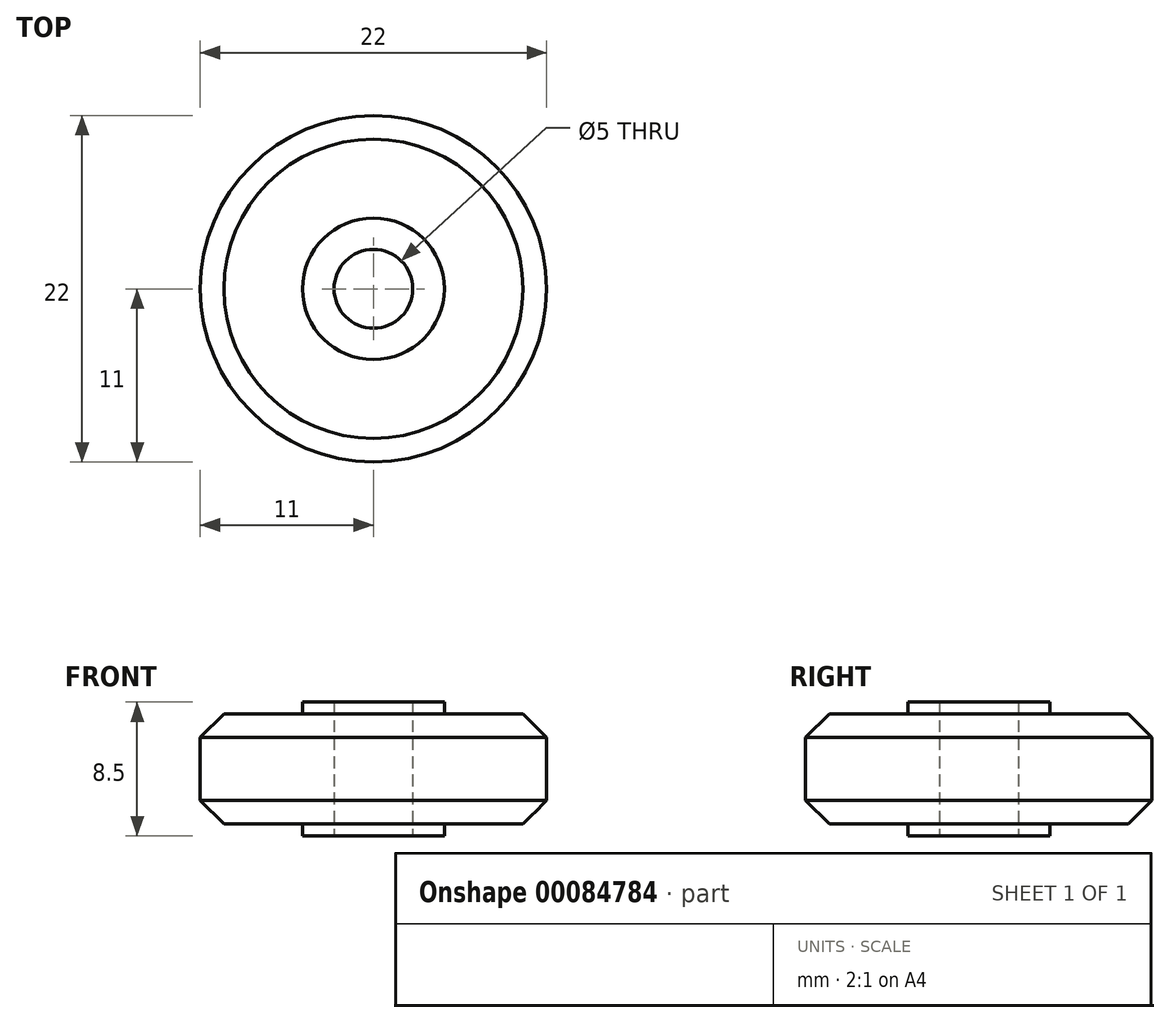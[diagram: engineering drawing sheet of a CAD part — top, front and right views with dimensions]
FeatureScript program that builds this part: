
annotation { "Feature Type Name" : "Feature", "Feature Type Description" : "" }
export const myFeature = defineFeature(function(context is Context, id is Id, definition is map)
    precondition{}
    {
        {
            var Q0;
            Q0=qCreatedBy(makeId("Top.planeOp"),FACE);
            var sketch = newSketch(context, id + "F0", { "sketchPlane" : qUnion([Q0])});
            skCircle(sketch, "E0", {"center": v(0, 0) * mm, "radius": 11 * mm});
            skCircle(sketch, "E1", {"center": v(0, 0) * mm, "radius": 2.5 * mm});
            skCircle(sketch, "E2", {"center": v(0, 0) * mm, "radius": 4.5 * mm});
            skSolve(sketch);
        }
        {
            var Q0;
            Q0=makeQuery(id+"F0.imprint","IMPRINT",FACE,{"disambiguationData":[TD([[makeQuery(id+"F0.imprint","IMPRINT",EDGE,{"derivedFrom":sQuery(id+"F0.wireOp",EDGE,"E1")}),-1.0]])]});
            extrude(context, id + "F1", {"entities" : qUnion([Q0]), "depth" : 4.25 * mm});
        }
        {
            var Q0;
            Q0=makeQuery(id+"F0.imprint","IMPRINT",FACE,{"disambiguationData":[TD([[makeQuery(id+"F0.imprint","IMPRINT",EDGE,{"derivedFrom":sQuery(id+"F0.wireOp",EDGE,"E0")}),1.0]])]});
            extrude(context, id + "F2", {"entities" : qUnion([Q0]), "operationType" : NewBodyOperationType.ADD, "depth" : 3.5 * mm});
        }
        {
            var Q0;
            Q0=makeQuery(id+"F2.opExtrude","CAP_EDGE",EDGE,{"disambiguationData":[OSD([sQuery(id+"F0.wireOp",EDGE,"E0")])],"isStart":false});
            chamfer(context, id + "F3", {"entities" : qUnion([Q0]), "width" : 1.5 * mm, "tangentPropagation" : true});
        }
        {
            var Q0;
            Q0=makeQuery(id+"F1.opExtrude","SWEPT_BODY",BODY,{"disambiguationData":[OSD([sQuery(id+"F0.wireOp",EDGE,"E1"),sQuery(id+"F0.wireOp",EDGE,"E2")])]});
            var Q1;
            {var subQ0=sQuery(id+"F0.wireOp",EDGE,"E2");Q1=makeQuery(id+"F2.boolean.opBoolean","MERGE",FACE,{"derivedFrom":[makeQuery(id+"F1.opExtrude","CAP_FACE",FACE,{"disambiguationData":[OSD([sQuery(id+"F0.wireOp",EDGE,"E1"),subQ0])],"isStart":true}),makeQuery(id+"F2.opExtrude","CAP_FACE",FACE,{"disambiguationData":[OSD([sQuery(id+"F0.wireOp",EDGE,"E0"),subQ0])],"isStart":true})]});}
            mirror(context, id + "F4", {"operationType" : NewBodyOperationType.ADD, "entities" : qUnion([Q0]), "mirrorPlane" : qUnion([Q1])});
        }
    });
